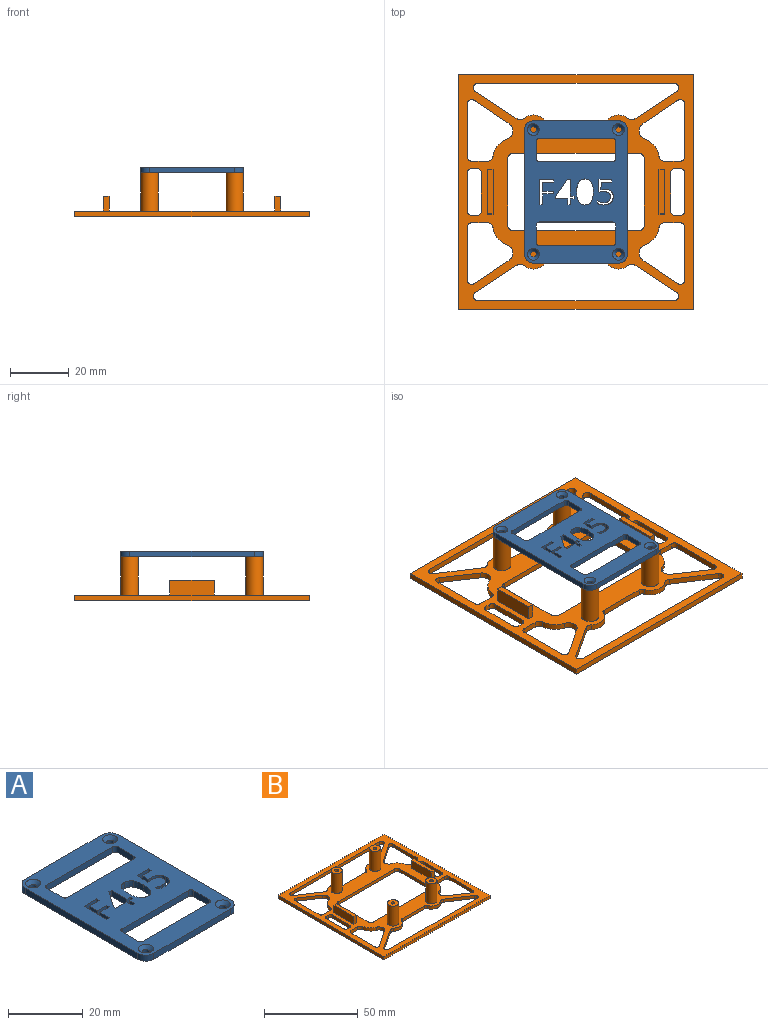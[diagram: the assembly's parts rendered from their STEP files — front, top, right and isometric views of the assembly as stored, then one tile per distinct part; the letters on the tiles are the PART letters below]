
ASSEMBLY  parts=2 mates=1
PART A: 82 faces, bbox 35x48.5x2 mm
  f0: plane 29x2mm, normal (0,1,0), area 58mm2, adj f64,f65,f68,f69
  f1: plane 42.5x2mm, normal (-1,0,0), area 85mm2, adj f64,f65,f67,f68
  f2: plane 29x2mm, normal (0,-1,0), area 58mm2, adj f64,f65,f66,f67
  f3: plane 6x2mm, normal (1,0,0), area 12mm2, adj f64,f65,f74,f77
  f4: plane 25x2mm, normal (0,-1,0), area 50mm2, adj f64,f65,f74,f75
  f5: plane 6x2mm, normal (-1,0,0), area 12mm2, adj f64,f65,f75,f76
  f6: plane 6x2mm, normal (1,0,0), area 12mm2, adj f64,f65,f70,f73
  f7: plane 25x2mm, normal (0,-1,0), area 50mm2, adj f64,f65,f70,f71
  f8: plane 6x2mm, normal (-1,0,0), area 12mm2, adj f64,f65,f71,f72
  f9: extruded ~3.29x2mm, area 6.8mm2, adj f10,f55,f64,f65
  f10: extruded ~3.33x2mm, area 6.9mm2, adj f9,f11,f64,f65
  f11: extruded ~2.15x2mm, area 5.1mm2, adj f10,f12,f64,f65
  f12: extruded ~2.11x2mm, area 5mm2, adj f11,f13,f64,f65
  f13: extruded ~3.31x2mm, area 6.9mm2, adj f12,f14,f64,f65
  f14: extruded ~3.34x2mm, area 6.9mm2, adj f13,f15,f64,f65
  f15: extruded ~2.14x2mm, area 5mm2, adj f14,f55,f64,f65
  f16: extruded ~2x1.35mm, area 2.7mm2, adj f17,f60,f64,f65
  f17: extruded ~2.14x2mm, area 4.6mm2, adj f16,f18,f64,f65
  f18: extruded ~2x1.85mm, area 4.1mm2, adj f17,f19,f64,f65
  f19: extruded ~2.1x2mm, area 4.7mm2, adj f18,f20,f64,f65
  f20: extruded ~2.35x2mm, area 5mm2, adj f19,f21,f64,f65
  f21: extruded ~2.22x2mm, area 4.6mm2, adj f20,f22,f64,f65
  f22: plane 2x0.94mm, normal (1,0,0), area 1.9mm2, adj f21,f23,f64,f65
  f23: extruded ~2x1.02mm, area 2.2mm2, adj f22,f24,f64,f65
  f24: extruded ~2x1.21mm, area 2.4mm2, adj f23,f25,f64,f65
  f25: extruded ~2x1.61mm, area 3.4mm2, adj f24,f26,f64,f65
  f26: extruded ~2x1.41mm, area 3.2mm2, adj f25,f27,f64,f65
  f27: extruded ~2.21x2mm, area 6.5mm2, adj f26,f28,f64,f65
  f28: extruded ~2x1.5mm, area 3mm2, adj f27,f29,f64,f65
  f29: plane 2x0.51mm, normal (0.54,0.84,0), area 1.2mm2, adj f28,f30,f64,f65
  f30: plane 4.03x2mm, normal (1,-0.08,0), area 8.1mm2, adj f29,f31,f64,f65
  f31: plane 4.28x2mm, normal (0,-1,0), area 8.6mm2, adj f30,f32,f64,f65
  f32: plane 2x0.9mm, normal (-1,0,0), area 1.8mm2, adj f31,f33,f64,f65
  f33: plane 3.45x2mm, normal (0,1,0), area 6.9mm2, adj f32,f60,f64,f65
  f34: plane 2x0.89mm, normal (-1,0,0), area 1.8mm2, adj f35,f61,f64,f65
  f35: plane 2x1.28mm, normal (0,1,0), area 2.6mm2, adj f34,f36,f64,f65
  f36: plane 2x1.98mm, normal (-1,0,0), area 4mm2, adj f35,f37,f64,f65
  f37: plane 2x0.94mm, normal (0,1,0), area 1.9mm2, adj f36,f38,f64,f65
  f38: plane 2x1.98mm, normal (1,0,0), area 4mm2, adj f37,f39,f64,f65
  f39: plane 4.19x2mm, normal (0,1,0), area 8.4mm2, adj f38,f40,f64,f65
  f40: plane 2x0.85mm, normal (1,0,0), area 1.7mm2, adj f39,f41,f64,f65
  f41: plane 5.83x4.09mm, normal (0.82,-0.57,0), area 14.2mm2, adj f40,f42,f64,f65
  f42: plane 2x1.04mm, normal (0,-1,0), area 2.1mm2, adj f41,f43,f64,f65
  f43: plane 5.79x2mm, normal (-1,0,0), area 11.6mm2, adj f42,f61,f64,f65
  f44: plane 3.68x2mm, normal (-1,0,0), area 7.4mm2, adj f45,f62,f64,f65
  f45: plane 2x1mm, normal (0,1,0), area 2mm2, adj f44,f46,f64,f65
  f46: plane 8.61x2mm, normal (1,0,0), area 17.2mm2, adj f45,f47,f64,f65
  f47: plane 4.8x2mm, normal (0,-1,0), area 9.6mm2, adj f46,f48,f64,f65
  f48: plane 2x0.89mm, normal (-1,0,0), area 1.8mm2, adj f47,f49,f64,f65
  f49: plane 3.8x2mm, normal (0,1,0), area 7.6mm2, adj f48,f50,f64,f65
  f50: plane 3.15x2mm, normal (-1,0,0), area 6.3mm2, adj f49,f51,f64,f65
  f51: plane 3.57x2mm, normal (0,-1,0), area 7.1mm2, adj f50,f52,f64,f65
  f52: plane 2x0.89mm, normal (-1,0,0), area 1.8mm2, adj f51,f62,f64,f65
  f53: plane 25x2mm, normal (0,1,0), area 50mm2, adj f64,f65,f76,f77
  f54: plane 25x2mm, normal (0,1,0), area 50mm2, adj f64,f65,f72,f73
  f55: extruded ~2.13x2mm, area 5.1mm2, adj f9,f15,f64,f65
  f56: cylinder r=1mm len=2mm, axis (0,0,-1), area 6.3mm2, adj f65,f79
  f57: cylinder r=1mm len=2mm, axis (0,0,-1), area 6.3mm2, adj f65,f78
  f58: cylinder r=1mm len=2mm, axis (0,0,-1), area 6.3mm2, adj f65,f81
  f59: cylinder r=1mm len=2mm, axis (0,0,-1), area 6.3mm2, adj f65,f80
  f60: plane 2.59x2mm, normal (-1,0.08,0), area 5.2mm2, adj f16,f33,f64,f65
  f61: plane 2x1.28mm, normal (0,-1,0), area 2.6mm2, adj f34,f43,f64,f65
  f62: plane 3.57x2mm, normal (0,1,0), area 7.1mm2, adj f44,f52,f64,f65
  f63: plane 42.5x2mm, normal (1,0,0), area 85mm2, adj f64,f65,f66,f69
  f64: plane 48.5x35mm, normal (0,0,1), area 1109.5mm2, adj f0,f1,f2,f3,f4,f5,f6,f7
  f65: plane 48.5x35mm, normal (0,0,-1), area 1147.2mm2, adj f0,f1,f2,f3,f4,f5,f6,f7
  f66: cylinder r=3mm len=3mm, axis (0,0,1), area 9.4mm2, adj f2,f63,f64,f65
  f67: cylinder r=3mm len=3mm, axis (0,0,-1), area 9.4mm2, adj f1,f2,f64,f65
  f68: cylinder r=3mm len=3mm, axis (0,0,1), area 9.4mm2, adj f0,f1,f64,f65
  f69: cylinder r=3mm len=3mm, axis (0,0,-1), area 9.4mm2, adj f0,f63,f64,f65
  f70: cylinder r=1mm len=2mm, axis (0,0,-1), area 3.1mm2, adj f6,f7,f64,f65
  f71: cylinder r=1mm len=2mm, axis (0,0,1), area 3.1mm2, adj f7,f8,f64,f65
  f72: cylinder r=1mm len=2mm, axis (0,0,-1), area 3.1mm2, adj f8,f54,f64,f65
  f73: cylinder r=1mm len=2mm, axis (0,0,1), area 3.1mm2, adj f6,f54,f64,f65
  f74: cylinder r=1mm len=2mm, axis (0,0,-1), area 3.1mm2, adj f3,f4,f64,f65
  f75: cylinder r=1mm len=2mm, axis (0,0,1), area 3.1mm2, adj f4,f5,f64,f65
  f76: cylinder r=1mm len=2mm, axis (0,0,-1), area 3.1mm2, adj f5,f53,f64,f65
  f77: cylinder r=1mm len=2mm, axis (0,0,1), area 3.1mm2, adj f3,f53,f64,f65
  f78: cone r=1mm half-angle=45deg, axis (0,0,1), area 13.3mm2, adj f57,f64
  f79: cone r=1mm half-angle=45deg, axis (0,0,1), area 13.3mm2, adj f56,f64
  f80: cone r=1mm half-angle=45deg, axis (0,0,1), area 13.3mm2, adj f59,f64
  f81: cone r=1mm half-angle=45deg, axis (0,0,1), area 13.3mm2, adj f58,f64
PART B: 112 faces, bbox 80x80x15 mm
  f0: plane 80x80mm, normal (0,0,1), area 2486.8mm2, adj f2,f3,f4,f5,f6,f7,f8,f9
  f1: plane 80x80mm, normal (0,0,-1), area 2659.9mm2, adj f2,f3,f4,f5,f32,f33,f34,f35
  f2: plane 80x2mm, normal (-1,0,0), area 160mm2, adj f0,f1,f3,f5
  f3: plane 80x2mm, normal (0,-1,0), area 160mm2, adj f0,f1,f2,f4
  f4: plane 80x2mm, normal (1,0,0), area 160mm2, adj f0,f1,f3,f5
  f5: plane 80x2mm, normal (0,1,0), area 160mm2, adj f0,f1,f2,f4
  f6: plane 5x2mm, normal (0,1,0), area 10mm2, adj f0,f7,f9,f10
  f7: plane 15x5mm, normal (-1,0,0), area 75mm2, adj f0,f6,f8,f10
  f8: plane 5x2mm, normal (0,-1,0), area 10mm2, adj f0,f7,f9,f10
  f9: plane 15x5mm, normal (1,0,0), area 75mm2, adj f0,f6,f8,f10
  f10: plane 15x2mm, normal (0,0,1), area 30mm2, adj f6,f7,f8,f9
  f11: plane 15x5mm, normal (1,0,0), area 75mm2, adj f0,f12,f14,f15
  f12: plane 5x2mm, normal (0,1,0), area 10mm2, adj f0,f11,f13,f15
  f13: plane 15x5mm, normal (-1,0,0), area 75mm2, adj f0,f12,f14,f15
  f14: plane 5x2mm, normal (0,-1,0), area 10mm2, adj f0,f11,f13,f15
  f15: plane 15x2mm, normal (0,0,1), area 30mm2, adj f11,f12,f13,f14
  f16: cylinder r=1mm len=13mm, axis (0,0,-1), area 81.7mm2, adj f18,f19
  f17: cylinder r=3mm len=13mm, axis (0,0,-1), area 245mm2, adj f0,f18
  f18: plane 6x6mm, normal (0,0,1), area 25.1mm2, adj f16,f17
  f19: plane 2x2mm, normal (0,0,1), area 3.1mm2, adj f16
  f20: cylinder r=1mm len=13mm, axis (0,0,-1), area 81.7mm2, adj f22,f23
  f21: cylinder r=3mm len=13mm, axis (0,0,-1), area 245mm2, adj f0,f22
  f22: plane 6x6mm, normal (0,0,1), area 25.1mm2, adj f20,f21
  f23: plane 2x2mm, normal (0,0,1), area 3.1mm2, adj f20
  f24: cylinder r=1mm len=13mm, axis (0,0,-1), area 81.7mm2, adj f26,f27
  f25: cylinder r=3mm len=13mm, axis (0,0,-1), area 245mm2, adj f0,f26
  f26: plane 6x6mm, normal (0,0,1), area 25.1mm2, adj f24,f25
  f27: plane 2x2mm, normal (0,0,1), area 3.1mm2, adj f24
  f28: cylinder r=1mm len=13mm, axis (0,0,-1), area 81.7mm2, adj f30,f31
  f29: cylinder r=3mm len=13mm, axis (0,0,-1), area 245mm2, adj f0,f30
  f30: plane 6x6mm, normal (0,0,1), area 25.1mm2, adj f28,f29
  f31: plane 2x2mm, normal (0,0,1), area 3.1mm2, adj f28
  f32: plane 22.5x2mm, normal (-1,0,0), area 45mm2, adj f0,f1,f33,f39
  f33: cylinder r=2mm len=2mm, axis (0,0,1), area 6.3mm2, adj f0,f1,f32,f34
  f34: plane 42.5x2mm, normal (0,-1,0), area 85mm2, adj f0,f1,f33,f35
  f35: cylinder r=2mm len=2mm, axis (0,0,1), area 6.3mm2, adj f0,f1,f34,f36
  f36: plane 22.5x2mm, normal (1,0,0), area 45mm2, adj f0,f1,f35,f37
  f37: cylinder r=2mm len=2mm, axis (0,0,1), area 6.3mm2, adj f0,f1,f36,f38
  f38: plane 42.5x2mm, normal (0,1,0), area 85mm2, adj f0,f1,f37,f39
  f39: cylinder r=2mm len=2mm, axis (0,0,1), area 6.3mm2, adj f0,f1,f32,f38
  f40: plane 2x1.75mm, normal (0,1,0), area 3.5mm2, adj f0,f1,f41,f47
  f41: cylinder r=1.5mm len=2mm, axis (0,0,1), area 4.7mm2, adj f0,f1,f40,f42
  f42: plane 13x2mm, normal (-1,0,0), area 26mm2, adj f0,f1,f41,f43
  f43: cylinder r=1.5mm len=2mm, axis (0,0,1), area 4.7mm2, adj f0,f1,f42,f44
  f44: plane 2x1.75mm, normal (0,-1,0), area 3.5mm2, adj f0,f1,f43,f45
  f45: cylinder r=1.5mm len=2mm, axis (0,0,1), area 4.7mm2, adj f0,f1,f44,f46
  f46: plane 13x2mm, normal (1,0,0), area 26mm2, adj f0,f1,f45,f47
  f47: cylinder r=1.5mm len=2mm, axis (0,0,1), area 4.7mm2, adj f0,f1,f40,f46
  f48: plane 2x1.75mm, normal (0,-1,0), area 3.5mm2, adj f0,f1,f49,f55
  f49: cylinder r=1.5mm len=2mm, axis (0,0,1), area 4.7mm2, adj f0,f1,f48,f50
  f50: plane 13x2mm, normal (1,0,0), area 26mm2, adj f0,f1,f49,f51
  f51: cylinder r=1.5mm len=2mm, axis (0,0,1), area 4.7mm2, adj f0,f1,f50,f52
  f52: plane 2x1.75mm, normal (0,1,0), area 3.5mm2, adj f0,f1,f51,f53
  f53: cylinder r=1.5mm len=2mm, axis (0,0,1), area 4.7mm2, adj f0,f1,f52,f54
  f54: plane 13x2mm, normal (-1,0,0), area 26mm2, adj f0,f1,f53,f55
  f55: cylinder r=1.5mm len=2mm, axis (0,0,1), area 4.7mm2, adj f0,f1,f48,f54
  f56: plane 67x2mm, normal (0,1,0), area 134mm2, adj f0,f1,f57,f67
  f57: cylinder r=1.5mm len=2.76mm, axis (0,0,1), area 7.7mm2, adj f0,f1,f56,f58
  f58: plane 14.22x9.31mm, normal (-0.55,-0.84,0), area 34mm2, adj f0,f1,f57,f59
  f59: cylinder r=2mm len=2.38mm, axis (0,0,1), area 5.1mm2, adj f0,f1,f58,f60
  f60: cylinder r=5mm len=7.91mm, axis (0,0,1), area 19.2mm2, adj f0,f1,f59,f61
  f61: cylinder r=1.5mm len=2mm, axis (0,0,1), area 3.7mm2, adj f0,f1,f60,f62
  f62: plane 16.8x2mm, normal (0,-1,0), area 33.6mm2, adj f0,f1,f61,f63
  f63: cylinder r=1.5mm len=2mm, axis (0,0,1), area 3.7mm2, adj f0,f1,f62,f64
  f64: cylinder r=5mm len=7.91mm, axis (0,0,1), area 19.2mm2, adj f0,f1,f63,f65
  f65: cylinder r=2mm len=2.38mm, axis (0,0,1), area 5.1mm2, adj f0,f1,f64,f66
  f66: plane 14.22x9.31mm, normal (0.55,-0.84,0), area 34mm2, adj f0,f1,f65,f67
  f67: cylinder r=1.5mm len=2.76mm, axis (0,0,1), area 7.7mm2, adj f0,f1,f56,f66
  f68: plane 11.84x7.96mm, normal (0.56,0.83,0), area 28.5mm2, adj f0,f1,f69,f75
  f69: cylinder r=1.5mm len=2.34mm, axis (0,0,1), area 6.5mm2, adj f0,f1,f68,f70
  f70: plane 18x2mm, normal (-1,0,0), area 36mm2, adj f0,f1,f69,f71
  f71: cylinder r=1.5mm len=2mm, axis (0,0,1), area 4.7mm2, adj f0,f1,f70,f72
  f72: plane 5.25x2mm, normal (0,-1,0), area 10.5mm2, adj f0,f1,f71,f73
  f73: cylinder r=2mm len=2mm, axis (0,0,1), area 5.7mm2, adj f0,f1,f72,f74
  f74: cylinder r=7.09mm len=5.73mm, axis (0,0,1), area 15.7mm2, adj f0,f1,f73,f75
  f75: cylinder r=3mm len=5.33mm, axis (0,0,1), area 13.3mm2, adj f0,f1,f68,f74
  f76: cylinder r=2mm len=2mm, axis (0,0,1), area 5.7mm2, adj f0,f1,f77,f83
  f77: cylinder r=7.09mm len=5.73mm, axis (0,0,1), area 15.7mm2, adj f0,f1,f76,f78
  f78: cylinder r=3mm len=5.33mm, axis (0,0,1), area 13.3mm2, adj f0,f1,f77,f79
  f79: plane 11.84x7.96mm, normal (-0.56,-0.83,0), area 28.5mm2, adj f0,f1,f78,f80
  f80: cylinder r=1.5mm len=2.34mm, axis (0,0,1), area 6.5mm2, adj f0,f1,f79,f81
  f81: plane 18x2mm, normal (1,0,0), area 36mm2, adj f0,f1,f80,f82
  f82: cylinder r=1.5mm len=2mm, axis (0,0,1), area 4.7mm2, adj f0,f1,f81,f83
  f83: plane 5.25x2mm, normal (0,1,0), area 10.5mm2, adj f0,f1,f76,f82
  f84: plane 67x2mm, normal (0,-1,0), area 134mm2, adj f0,f1,f85,f95
  f85: cylinder r=1.5mm len=2.76mm, axis (0,0,1), area 7.7mm2, adj f0,f1,f84,f86
  f86: plane 14.22x9.31mm, normal (0.55,0.84,0), area 34mm2, adj f0,f1,f85,f87
  f87: cylinder r=2mm len=2.38mm, axis (0,0,1), area 5.1mm2, adj f0,f1,f86,f88
  f88: cylinder r=5mm len=7.91mm, axis (0,0,1), area 19.2mm2, adj f0,f1,f87,f89
  f89: cylinder r=1.5mm len=2mm, axis (0,0,1), area 3.7mm2, adj f0,f1,f88,f90
  f90: plane 16.8x2mm, normal (0,1,0), area 33.6mm2, adj f0,f1,f89,f91
  f91: cylinder r=1.5mm len=2mm, axis (0,0,1), area 3.7mm2, adj f0,f1,f90,f92
  f92: cylinder r=5mm len=7.91mm, axis (0,0,1), area 19.2mm2, adj f0,f1,f91,f93
  f93: cylinder r=2mm len=2.38mm, axis (0,0,1), area 5.1mm2, adj f0,f1,f92,f94
  f94: plane 14.22x9.31mm, normal (-0.55,0.84,0), area 34mm2, adj f0,f1,f93,f95
  f95: cylinder r=1.5mm len=2.76mm, axis (0,0,1), area 7.7mm2, adj f0,f1,f84,f94
  f96: cylinder r=1.5mm len=2.34mm, axis (0,0,1), area 6.5mm2, adj f0,f1,f97,f103
  f97: plane 11.84x7.96mm, normal (0.56,-0.83,0), area 28.5mm2, adj f0,f1,f96,f98
  f98: cylinder r=3mm len=5.33mm, axis (0,0,1), area 13.3mm2, adj f0,f1,f97,f99
  f99: cylinder r=7.09mm len=5.73mm, axis (0,0,1), area 15.7mm2, adj f0,f1,f98,f100
  f100: cylinder r=2mm len=2mm, axis (0,0,1), area 5.7mm2, adj f0,f1,f99,f101
  f101: plane 5.25x2mm, normal (0,1,0), area 10.5mm2, adj f0,f1,f100,f102
  f102: cylinder r=1.5mm len=2mm, axis (0,0,1), area 4.7mm2, adj f0,f1,f101,f103
  f103: plane 18x2mm, normal (-1,0,0), area 36mm2, adj f0,f1,f96,f102
  f104: cylinder r=1.5mm len=2.34mm, axis (0,0,1), area 6.5mm2, adj f0,f1,f105,f111
  f105: plane 11.84x7.96mm, normal (-0.56,0.83,0), area 28.5mm2, adj f0,f1,f104,f106
  f106: cylinder r=3mm len=5.33mm, axis (0,0,1), area 13.3mm2, adj f0,f1,f105,f107
  f107: cylinder r=7.09mm len=5.73mm, axis (0,0,1), area 15.7mm2, adj f0,f1,f106,f108
  f108: cylinder r=2mm len=2mm, axis (0,0,1), area 5.7mm2, adj f0,f1,f107,f109
  f109: plane 5.25x2mm, normal (0,-1,0), area 10.5mm2, adj f0,f1,f108,f110
  f110: cylinder r=1.5mm len=2mm, axis (0,0,1), area 4.7mm2, adj f0,f1,f109,f111
  f111: plane 18x2mm, normal (1,0,0), area 36mm2, adj f0,f1,f104,f110
PLACE A t=(-3.44,0.1,26.5)mm
PLACE B t=(-3.44,0.1,11.5)mm
MATE cylindrical B.f24 <-> A.f58  axis (0,0,1) through (-17.94,-21.15,26.5)mm
